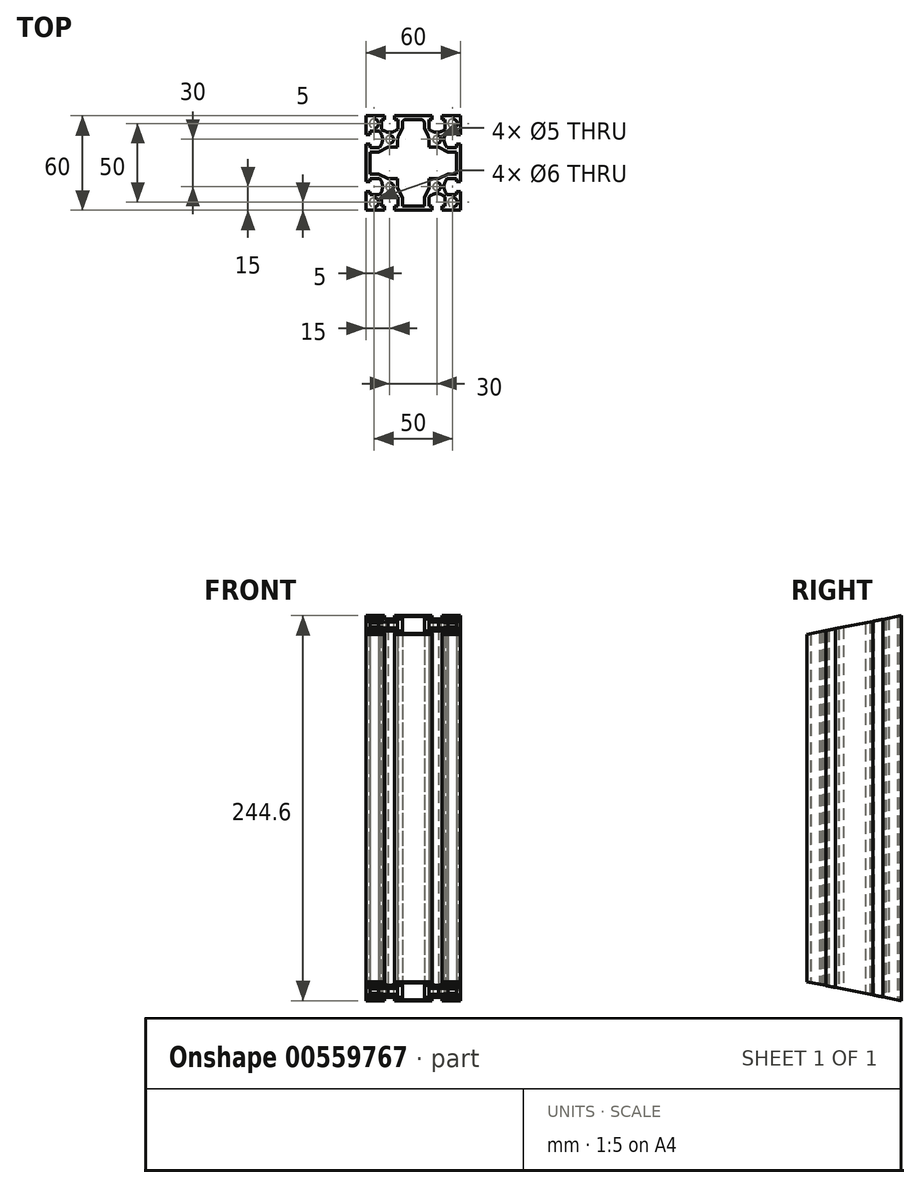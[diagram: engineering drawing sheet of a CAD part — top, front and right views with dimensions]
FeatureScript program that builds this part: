
annotation { "Feature Type Name" : "Feature", "Feature Type Description" : "" }
export const myFeature = defineFeature(function(context is Context, id is Id, definition is map)
    precondition{}
    {
        {
            var Q0;
            Q0=qCreatedBy(makeId("Top.planeOp"),FACE);
            var sketch = newSketch(context, id + "F0", { "sketchPlane" : qUnion([Q0])});
            skLineSegment(sketch, "E0.bottom", {"start": v(30, -30) * mm, "end": v(-30, -30) * mm});
            skLineSegment(sketch, "E0.top", {"start": v(30, 30) * mm, "end": v(-30, 30) * mm});
            skLineSegment(sketch, "E0.left", {"start": v(30, -30) * mm, "end": v(30, 30) * mm});
            skLineSegment(sketch, "E0.right", {"start": v(-30, -30) * mm, "end": v(-30, 30) * mm});
            skPoint(sketch, "E0.middle", {"position": v(0, 0) * mm});
            skLineSegment(sketch, "E1.top", {"start": v(-11.85, 30) * mm, "end": v(-18.15, 30) * mm});
            skLineSegment(sketch, "E1.left", {"start": v(-11.85, 27.5) * mm, "end": v(-11.85, 30) * mm});
            skLineSegment(sketch, "E1.right", {"start": v(-18.15, 27.5) * mm, "end": v(-18.15, 30) * mm});
            skPoint(sketch, "E1.middle", {"position": v(-15, 28.75) * mm});
            skLineSegment(sketch, "E2.bottom", {"start": v(-9.85, 27.5) * mm, "end": v(-11.85, 27.5) * mm});
            skLineSegment(sketch, "E2.left", {"start": v(-9.85, 27.5) * mm, "end": v(-9.85, 21.55) * mm});
            skLineSegment(sketch, "E2.right", {"start": v(-20.15, 27.5) * mm, "end": v(-20.15, 21.55) * mm});
            skPoint(sketch, "E2.middle", {"position": v(-15, 24.52) * mm});
            skArc(sketch, "E3", {"start": v(-20.15, 21.55) * mm, "mid": v(-15, 19.5) * mm, "end": v(-9.85, 21.55) * mm});
            skPoint(sketch, "E4.MirrorP", {"position": v(15, 24.52) * mm});
            skPoint(sketch, "E5.MirrorP", {"position": v(15, 28.75) * mm});
            skLineSegment(sketch, "E6.MirrorCS", {"start": v(11.85, 27.5) * mm, "end": v(11.85, 30) * mm});
            skLineSegment(sketch, "E7.MirrorCS", {"start": v(18.15, 27.5) * mm, "end": v(18.15, 30) * mm});
            skLineSegment(sketch, "E8.MirrorCS", {"start": v(9.85, 27.5) * mm, "end": v(11.85, 27.5) * mm});
            skLineSegment(sketch, "E9.MirrorCS", {"start": v(9.85, 27.5) * mm, "end": v(9.85, 21.55) * mm});
            skArc(sketch, "E10.MirrorCS", {"start": v(20.15, 21.55) * mm, "mid": v(15, 19.5) * mm, "end": v(9.85, 21.55) * mm});
            skLineSegment(sketch, "E11.MirrorCS", {"start": v(20.15, 27.5) * mm, "end": v(20.15, 21.55) * mm});
            skLineSegment(sketch, "E12.MirrorCS", {"start": v(11.85, 30) * mm, "end": v(18.15, 30) * mm});
            skLineSegment(sketch, "E13.1.0", {"start": v(27.5, 20.15) * mm, "end": v(21.55, 20.15) * mm});
            skLineSegment(sketch, "E13.1.1", {"start": v(27.5, 9.85) * mm, "end": v(21.55, 9.85) * mm});
            skArc(sketch, "E13.1.2", {"start": v(21.55, 20.15) * mm, "mid": v(19.5, 15) * mm, "end": v(21.55, 9.85) * mm});
            skLineSegment(sketch, "E13.1.3", {"start": v(27.5, -9.85) * mm, "end": v(21.55, -9.85) * mm});
            skLineSegment(sketch, "E13.1.4", {"start": v(27.5, -20.15) * mm, "end": v(21.55, -20.15) * mm});
            skPoint(sketch, "E13.1.5", {"position": v(28.75, 15) * mm});
            skPoint(sketch, "E13.1.6", {"position": v(28.75, -15) * mm});
            skArc(sketch, "E13.1.7", {"start": v(21.55, -20.15) * mm, "mid": v(19.5, -15) * mm, "end": v(21.55, -9.85) * mm});
            skPoint(sketch, "E13.1.8", {"position": v(24.52, -15) * mm});
            skPoint(sketch, "E13.1.9", {"position": v(24.52, 15) * mm});
            skLineSegment(sketch, "E13.1.10", {"start": v(27.5, 9.85) * mm, "end": v(27.5, 20.15) * mm});
            skLineSegment(sketch, "E13.1.11", {"start": v(27.5, -11.85) * mm, "end": v(27.5, -18.15) * mm});
            skLineSegment(sketch, "E13.1.12", {"start": v(30, 11.85) * mm, "end": v(30, 18.15) * mm});
            skLineSegment(sketch, "E13.1.13", {"start": v(30, -11.85) * mm, "end": v(30, -18.15) * mm});
            skLineSegment(sketch, "E13.1.14", {"start": v(27.5, 18.15) * mm, "end": v(30, 18.15) * mm});
            skLineSegment(sketch, "E13.1.15", {"start": v(27.5, 11.85) * mm, "end": v(30, 11.85) * mm});
            skLineSegment(sketch, "E13.1.16", {"start": v(27.5, 11.85) * mm, "end": v(27.5, 18.15) * mm});
            skLineSegment(sketch, "E13.1.17", {"start": v(27.5, -9.85) * mm, "end": v(27.5, -20.15) * mm});
            skLineSegment(sketch, "E13.1.18", {"start": v(27.5, -18.15) * mm, "end": v(30, -18.15) * mm});
            skLineSegment(sketch, "E13.1.19", {"start": v(27.5, -11.85) * mm, "end": v(30, -11.85) * mm});
            skLineSegment(sketch, "E13.2.0", {"start": v(20.15, -27.5) * mm, "end": v(20.15, -21.55) * mm});
            skLineSegment(sketch, "E13.2.1", {"start": v(9.85, -27.5) * mm, "end": v(9.85, -21.55) * mm});
            skArc(sketch, "E13.2.2", {"start": v(20.15, -21.55) * mm, "mid": v(15, -19.5) * mm, "end": v(9.85, -21.55) * mm});
            skLineSegment(sketch, "E13.2.3", {"start": v(-9.85, -27.5) * mm, "end": v(-9.85, -21.55) * mm});
            skLineSegment(sketch, "E13.2.4", {"start": v(-20.15, -27.5) * mm, "end": v(-20.15, -21.55) * mm});
            skPoint(sketch, "E13.2.5", {"position": v(15, -28.75) * mm});
            skPoint(sketch, "E13.2.6", {"position": v(-15, -28.75) * mm});
            skArc(sketch, "E13.2.7", {"start": v(-20.15, -21.55) * mm, "mid": v(-15, -19.5) * mm, "end": v(-9.85, -21.55) * mm});
            skPoint(sketch, "E13.2.8", {"position": v(-15, -24.52) * mm});
            skPoint(sketch, "E13.2.9", {"position": v(15, -24.52) * mm});
            skLineSegment(sketch, "E13.2.10", {"start": v(9.85, -27.5) * mm, "end": v(20.15, -27.5) * mm});
            skLineSegment(sketch, "E13.2.11", {"start": v(-11.85, -27.5) * mm, "end": v(-18.15, -27.5) * mm});
            skLineSegment(sketch, "E13.2.12", {"start": v(11.85, -30) * mm, "end": v(18.15, -30) * mm});
            skLineSegment(sketch, "E13.2.13", {"start": v(-11.85, -30) * mm, "end": v(-18.15, -30) * mm});
            skLineSegment(sketch, "E13.2.14", {"start": v(18.15, -27.5) * mm, "end": v(18.15, -30) * mm});
            skLineSegment(sketch, "E13.2.15", {"start": v(11.85, -27.5) * mm, "end": v(11.85, -30) * mm});
            skLineSegment(sketch, "E13.2.16", {"start": v(11.85, -27.5) * mm, "end": v(18.15, -27.5) * mm});
            skLineSegment(sketch, "E13.2.17", {"start": v(-9.85, -27.5) * mm, "end": v(-20.15, -27.5) * mm});
            skLineSegment(sketch, "E13.2.18", {"start": v(-18.15, -27.5) * mm, "end": v(-18.15, -30) * mm});
            skLineSegment(sketch, "E13.2.19", {"start": v(-11.85, -27.5) * mm, "end": v(-11.85, -30) * mm});
            skLineSegment(sketch, "E13.3.0", {"start": v(-27.5, -20.15) * mm, "end": v(-21.55, -20.15) * mm});
            skLineSegment(sketch, "E13.3.1", {"start": v(-27.5, -9.85) * mm, "end": v(-21.55, -9.85) * mm});
            skArc(sketch, "E13.3.2", {"start": v(-21.55, -20.15) * mm, "mid": v(-19.5, -15) * mm, "end": v(-21.55, -9.85) * mm});
            skLineSegment(sketch, "E13.3.3", {"start": v(-27.5, 9.85) * mm, "end": v(-21.55, 9.85) * mm});
            skLineSegment(sketch, "E13.3.4", {"start": v(-27.5, 20.15) * mm, "end": v(-21.55, 20.15) * mm});
            skPoint(sketch, "E13.3.5", {"position": v(-28.75, -15) * mm});
            skPoint(sketch, "E13.3.6", {"position": v(-28.75, 15) * mm});
            skArc(sketch, "E13.3.7", {"start": v(-21.55, 20.15) * mm, "mid": v(-19.5, 15) * mm, "end": v(-21.55, 9.85) * mm});
            skPoint(sketch, "E13.3.8", {"position": v(-24.52, 15) * mm});
            skPoint(sketch, "E13.3.9", {"position": v(-24.52, -15) * mm});
            skLineSegment(sketch, "E13.3.10", {"start": v(-27.5, -9.85) * mm, "end": v(-27.5, -20.15) * mm});
            skLineSegment(sketch, "E13.3.11", {"start": v(-27.5, 11.85) * mm, "end": v(-27.5, 18.15) * mm});
            skLineSegment(sketch, "E13.3.12", {"start": v(-30, -11.85) * mm, "end": v(-30, -18.15) * mm});
            skLineSegment(sketch, "E13.3.13", {"start": v(-30, 11.85) * mm, "end": v(-30, 18.15) * mm});
            skLineSegment(sketch, "E13.3.14", {"start": v(-27.5, -18.15) * mm, "end": v(-30, -18.15) * mm});
            skLineSegment(sketch, "E13.3.15", {"start": v(-27.5, -11.85) * mm, "end": v(-30, -11.85) * mm});
            skLineSegment(sketch, "E13.3.16", {"start": v(-27.5, -11.85) * mm, "end": v(-27.5, -18.15) * mm});
            skLineSegment(sketch, "E13.3.17", {"start": v(-27.5, 9.85) * mm, "end": v(-27.5, 20.15) * mm});
            skLineSegment(sketch, "E13.3.18", {"start": v(-27.5, 18.15) * mm, "end": v(-30, 18.15) * mm});
            skLineSegment(sketch, "E13.3.19", {"start": v(-27.5, 11.85) * mm, "end": v(-30, 11.85) * mm});
            skLineSegment(sketch, "E13.anchor1", {"start": v(0, 0) * mm, "end": v(-20.15, 21.55) * mm, "construction": true});
            skLineSegment(sketch, "E13.anchor2", {"start": v(0, 0) * mm, "end": v(-21.55, -20.15) * mm, "construction": true});
            skLineSegment(sketch, "E14.trimOffspring", {"start": v(-18.15, 27.5) * mm, "end": v(-20.15, 27.5) * mm});
            skLineSegment(sketch, "E15.trimOffspring", {"start": v(18.15, 27.5) * mm, "end": v(20.15, 27.5) * mm});
            skCircle(sketch, "E16", {"center": v(-15, 15) * mm, "radius": 2.5 * mm});
            skCircle(sketch, "E17", {"center": v(-25, 25) * mm, "radius": 3 * mm});
            skCircle(sketch, "E18.MirrorC", {"center": v(25, 25) * mm, "radius": 3 * mm});
            skCircle(sketch, "E19.MirrorC", {"center": v(25, -25) * mm, "radius": 3 * mm});
            skCircle(sketch, "E20.MirrorC", {"center": v(-25, -25) * mm, "radius": 3 * mm});
            skCircle(sketch, "E21.MirrorC", {"center": v(15, 15) * mm, "radius": 2.5 * mm});
            skCircle(sketch, "E22.MirrorC", {"center": v(15, -15) * mm, "radius": 2.5 * mm});
            skCircle(sketch, "E23.MirrorC", {"center": v(-15, -15) * mm, "radius": 2.5 * mm});
            skLineSegment(sketch, "E24", {"start": v(-7, 27.5) * mm, "end": v(0, 27.5) * mm});
            skLineSegment(sketch, "E25", {"start": v(-7, 27.5) * mm, "end": v(-7, 22) * mm});
            skLineSegment(sketch, "E26", {"start": v(-10, 10) * mm, "end": v(-10, 16) * mm});
            skLineSegment(sketch, "E27", {"start": v(-10, 16) * mm, "end": v(-7, 22) * mm});
            skLineSegment(sketch, "E28.MirrorCS", {"start": v(10, 10) * mm, "end": v(10, 16) * mm});
            skLineSegment(sketch, "E29.MirrorCS", {"start": v(10, 16) * mm, "end": v(7, 22) * mm});
            skLineSegment(sketch, "E30.MirrorCS", {"start": v(7, 27.5) * mm, "end": v(0, 27.5) * mm});
            skLineSegment(sketch, "E31.MirrorCS", {"start": v(7, 27.5) * mm, "end": v(7, 22) * mm});
            skLineSegment(sketch, "E32.1.0", {"start": v(-10, -10) * mm, "end": v(-16, -10) * mm});
            skLineSegment(sketch, "E32.1.1", {"start": v(-16, -10) * mm, "end": v(-22, -7) * mm});
            skLineSegment(sketch, "E32.1.2", {"start": v(-27.5, -7) * mm, "end": v(-22, -7) * mm});
            skLineSegment(sketch, "E32.1.3", {"start": v(-27.5, -7) * mm, "end": v(-27.5, 0) * mm});
            skLineSegment(sketch, "E32.1.4", {"start": v(-27.5, 7) * mm, "end": v(-27.5, 0) * mm});
            skLineSegment(sketch, "E32.1.5", {"start": v(-27.5, 7) * mm, "end": v(-22, 7) * mm});
            skLineSegment(sketch, "E32.1.6", {"start": v(-16, 10) * mm, "end": v(-22, 7) * mm});
            skLineSegment(sketch, "E32.1.7", {"start": v(-10, 10) * mm, "end": v(-16, 10) * mm});
            skLineSegment(sketch, "E32.2.0", {"start": v(10, -10) * mm, "end": v(10, -16) * mm});
            skLineSegment(sketch, "E32.2.1", {"start": v(10, -16) * mm, "end": v(7, -22) * mm});
            skLineSegment(sketch, "E32.2.2", {"start": v(7, -27.5) * mm, "end": v(7, -22) * mm});
            skLineSegment(sketch, "E32.2.3", {"start": v(7, -27.5) * mm, "end": v(0, -27.5) * mm});
            skLineSegment(sketch, "E32.2.4", {"start": v(-7, -27.5) * mm, "end": v(0, -27.5) * mm});
            skLineSegment(sketch, "E32.2.5", {"start": v(-7, -27.5) * mm, "end": v(-7, -22) * mm});
            skLineSegment(sketch, "E32.2.6", {"start": v(-10, -16) * mm, "end": v(-7, -22) * mm});
            skLineSegment(sketch, "E32.2.7", {"start": v(-10, -10) * mm, "end": v(-10, -16) * mm});
            skLineSegment(sketch, "E32.3.0", {"start": v(10, 10) * mm, "end": v(16, 10) * mm});
            skLineSegment(sketch, "E32.3.1", {"start": v(16, 10) * mm, "end": v(22, 7) * mm});
            skLineSegment(sketch, "E32.3.2", {"start": v(27.5, 7) * mm, "end": v(22, 7) * mm});
            skLineSegment(sketch, "E32.3.3", {"start": v(27.5, 7) * mm, "end": v(27.5, 0) * mm});
            skLineSegment(sketch, "E32.3.4", {"start": v(27.5, -7) * mm, "end": v(27.5, 0) * mm});
            skLineSegment(sketch, "E32.3.5", {"start": v(27.5, -7) * mm, "end": v(22, -7) * mm});
            skLineSegment(sketch, "E32.3.6", {"start": v(16, -10) * mm, "end": v(22, -7) * mm});
            skLineSegment(sketch, "E32.3.7", {"start": v(10, -10) * mm, "end": v(16, -10) * mm});
            skSolve(sketch);
        }
        {
            var Q0;
            {var subQ30=sQuery(id+"F0.wireOp",EDGE,"E1.left");Q0=makeQuery(id+"F0.imprint","IMPRINT",FACE,{"disambiguationData":[TD([[makeQuery(id+"F0.imprint","IMPRINT",EDGE,{"derivedFrom":subQ30}),-1.0]])]});}
            extrude(context, id + "F1", {"entities" : qUnion([Q0]), "depth" : 244.6 * mm, "offsetDistance" : 25 * mm});
        }
        {
            var Q0;
            Q0=makeQuery(id+"F1.opExtrude","SWEPT_EDGE",EDGE,{"disambiguationData":[OSD([sQuery(id+"F0.wireOp",EDGE,"E24"),sQuery(id+"F0.wireOp",EDGE,"E25")])]});
            var Q1;
            Q1=makeQuery(id+"F1.opExtrude","SWEPT_EDGE",EDGE,{"disambiguationData":[OSD([sQuery(id+"F0.wireOp",EDGE,"E30.MirrorCS"),sQuery(id+"F0.wireOp",EDGE,"E31.MirrorCS")])]});
            var Q2;
            Q2=makeQuery(id+"F1.opExtrude","SWEPT_EDGE",EDGE,{"disambiguationData":[OSD([sQuery(id+"F0.wireOp",EDGE,"840db5bc-c403-45cd-90c7-254e62d9e8c5.3.2"),sQuery(id+"F0.wireOp",EDGE,"840db5bc-c403-45cd-90c7-254e62d9e8c5.3.3")])]});
            var Q3;
            Q3=makeQuery(id+"F1.opExtrude","SWEPT_EDGE",EDGE,{"disambiguationData":[OSD([sQuery(id+"F0.wireOp",EDGE,"840db5bc-c403-45cd-90c7-254e62d9e8c5.3.4"),sQuery(id+"F0.wireOp",EDGE,"840db5bc-c403-45cd-90c7-254e62d9e8c5.3.5")])]});
            var Q4;
            Q4=makeQuery(id+"F1.opExtrude","SWEPT_EDGE",EDGE,{"disambiguationData":[OSD([sQuery(id+"F0.wireOp",EDGE,"840db5bc-c403-45cd-90c7-254e62d9e8c5.1.4"),sQuery(id+"F0.wireOp",EDGE,"840db5bc-c403-45cd-90c7-254e62d9e8c5.1.5")])]});
            var Q5;
            Q5=makeQuery(id+"F1.opExtrude","SWEPT_EDGE",EDGE,{"disambiguationData":[OSD([sQuery(id+"F0.wireOp",EDGE,"840db5bc-c403-45cd-90c7-254e62d9e8c5.1.2"),sQuery(id+"F0.wireOp",EDGE,"840db5bc-c403-45cd-90c7-254e62d9e8c5.1.3")])]});
            var Q6;
            Q6=makeQuery(id+"F1.opExtrude","SWEPT_EDGE",EDGE,{"disambiguationData":[OSD([sQuery(id+"F0.wireOp",EDGE,"840db5bc-c403-45cd-90c7-254e62d9e8c5.2.2"),sQuery(id+"F0.wireOp",EDGE,"840db5bc-c403-45cd-90c7-254e62d9e8c5.2.3")])]});
            var Q7;
            Q7=makeQuery(id+"F1.opExtrude","SWEPT_EDGE",EDGE,{"disambiguationData":[OSD([sQuery(id+"F0.wireOp",EDGE,"840db5bc-c403-45cd-90c7-254e62d9e8c5.2.4"),sQuery(id+"F0.wireOp",EDGE,"840db5bc-c403-45cd-90c7-254e62d9e8c5.2.5")])]});
            fillet(context, id + "F2", {"entities" : qUnion([Q0, Q1, Q2, Q3, Q4, Q5, Q6, Q7]), "radius" : 2 * mm, "tangentPropagation" : true, "allowEdgeOverflow" : false});
        }
        {
            var Q0;
            Q0=makeQuery(id+"F1.opExtrude","SWEPT_EDGE",EDGE,{"disambiguationData":[OSD([sQuery(id+"F0.wireOp",EDGE,"E26"),sQuery(id+"F0.wireOp",EDGE,"E27")])]});
            var Q1;
            Q1=makeQuery(id+"F1.opExtrude","SWEPT_EDGE",EDGE,{"disambiguationData":[OSD([sQuery(id+"F0.wireOp",EDGE,"E28.MirrorCS"),sQuery(id+"F0.wireOp",EDGE,"E29.MirrorCS")])]});
            var Q2;
            Q2=makeQuery(id+"F1.opExtrude","SWEPT_EDGE",EDGE,{"disambiguationData":[OSD([sQuery(id+"F0.wireOp",EDGE,"840db5bc-c403-45cd-90c7-254e62d9e8c5.3.0"),sQuery(id+"F0.wireOp",EDGE,"840db5bc-c403-45cd-90c7-254e62d9e8c5.3.1")])]});
            var Q3;
            Q3=makeQuery(id+"F1.opExtrude","SWEPT_EDGE",EDGE,{"disambiguationData":[OSD([sQuery(id+"F0.wireOp",EDGE,"840db5bc-c403-45cd-90c7-254e62d9e8c5.1.6"),sQuery(id+"F0.wireOp",EDGE,"840db5bc-c403-45cd-90c7-254e62d9e8c5.1.7")])]});
            var Q4;
            Q4=makeQuery(id+"F1.opExtrude","SWEPT_EDGE",EDGE,{"disambiguationData":[OSD([sQuery(id+"F0.wireOp",EDGE,"840db5bc-c403-45cd-90c7-254e62d9e8c5.1.0"),sQuery(id+"F0.wireOp",EDGE,"840db5bc-c403-45cd-90c7-254e62d9e8c5.1.1")])]});
            var Q5;
            Q5=makeQuery(id+"F1.opExtrude","SWEPT_EDGE",EDGE,{"disambiguationData":[OSD([sQuery(id+"F0.wireOp",EDGE,"840db5bc-c403-45cd-90c7-254e62d9e8c5.3.6"),sQuery(id+"F0.wireOp",EDGE,"840db5bc-c403-45cd-90c7-254e62d9e8c5.3.7")])]});
            var Q6;
            Q6=makeQuery(id+"F1.opExtrude","SWEPT_EDGE",EDGE,{"disambiguationData":[OSD([sQuery(id+"F0.wireOp",EDGE,"840db5bc-c403-45cd-90c7-254e62d9e8c5.2.0"),sQuery(id+"F0.wireOp",EDGE,"840db5bc-c403-45cd-90c7-254e62d9e8c5.2.1")])]});
            var Q7;
            Q7=makeQuery(id+"F1.opExtrude","SWEPT_EDGE",EDGE,{"disambiguationData":[OSD([sQuery(id+"F0.wireOp",EDGE,"840db5bc-c403-45cd-90c7-254e62d9e8c5.2.6"),sQuery(id+"F0.wireOp",EDGE,"840db5bc-c403-45cd-90c7-254e62d9e8c5.2.7")])]});
            fillet(context, id + "F3", {"entities" : qUnion([Q0, Q1, Q2, Q3, Q4, Q5, Q6, Q7]), "radius" : 7 * mm, "tangentPropagation" : true, "allowEdgeOverflow" : false});
        }
        {
            var Q0;
            Q0=qCreatedBy(makeId("Right.planeOp"),FACE);
            var sketch = newSketch(context, id + "F4", { "sketchPlane" : qUnion([Q0])});
            skLineSegment(sketch, "E33.bottom", {"start": v(30, 0) * mm, "end": v(-94.02, 24.67) * mm});
            skLineSegment(sketch, "E33.top", {"start": v(6.06, -120.36) * mm, "end": v(-117.96, -95.69) * mm});
            skLineSegment(sketch, "E33.left", {"start": v(30, 0) * mm, "end": v(6.06, -120.36) * mm});
            skLineSegment(sketch, "E33.right", {"start": v(-94.02, 24.67) * mm, "end": v(-117.96, -95.69) * mm});
            skLineSegment(sketch, "E34.bottom", {"start": v(11.53, 337.46) * mm, "end": v(-122.88, 310.72) * mm});
            skLineSegment(sketch, "E34.top", {"start": v(30, 244.6) * mm, "end": v(-104.4, 217.86) * mm});
            skLineSegment(sketch, "E34.left", {"start": v(11.53, 337.46) * mm, "end": v(30, 244.6) * mm});
            skLineSegment(sketch, "E34.right", {"start": v(-122.88, 310.72) * mm, "end": v(-104.4, 217.86) * mm});
            skSolve(sketch);
        }
        {
            var Q0;
            Q0=qSketchRegion(id+"F4",true);
            extrude(context, id + "F5", {"entities" : qUnion([Q0]), "operationType" : NewBodyOperationType.REMOVE, "oppositeDirection" : true, "depth" : 30 * mm, "offsetDistance" : 25 * mm, "hasSecondDirection" : true, "secondDirectionOppositeDirection" : false, "secondDirectionDepth" : 30 * mm});
        }
    });
